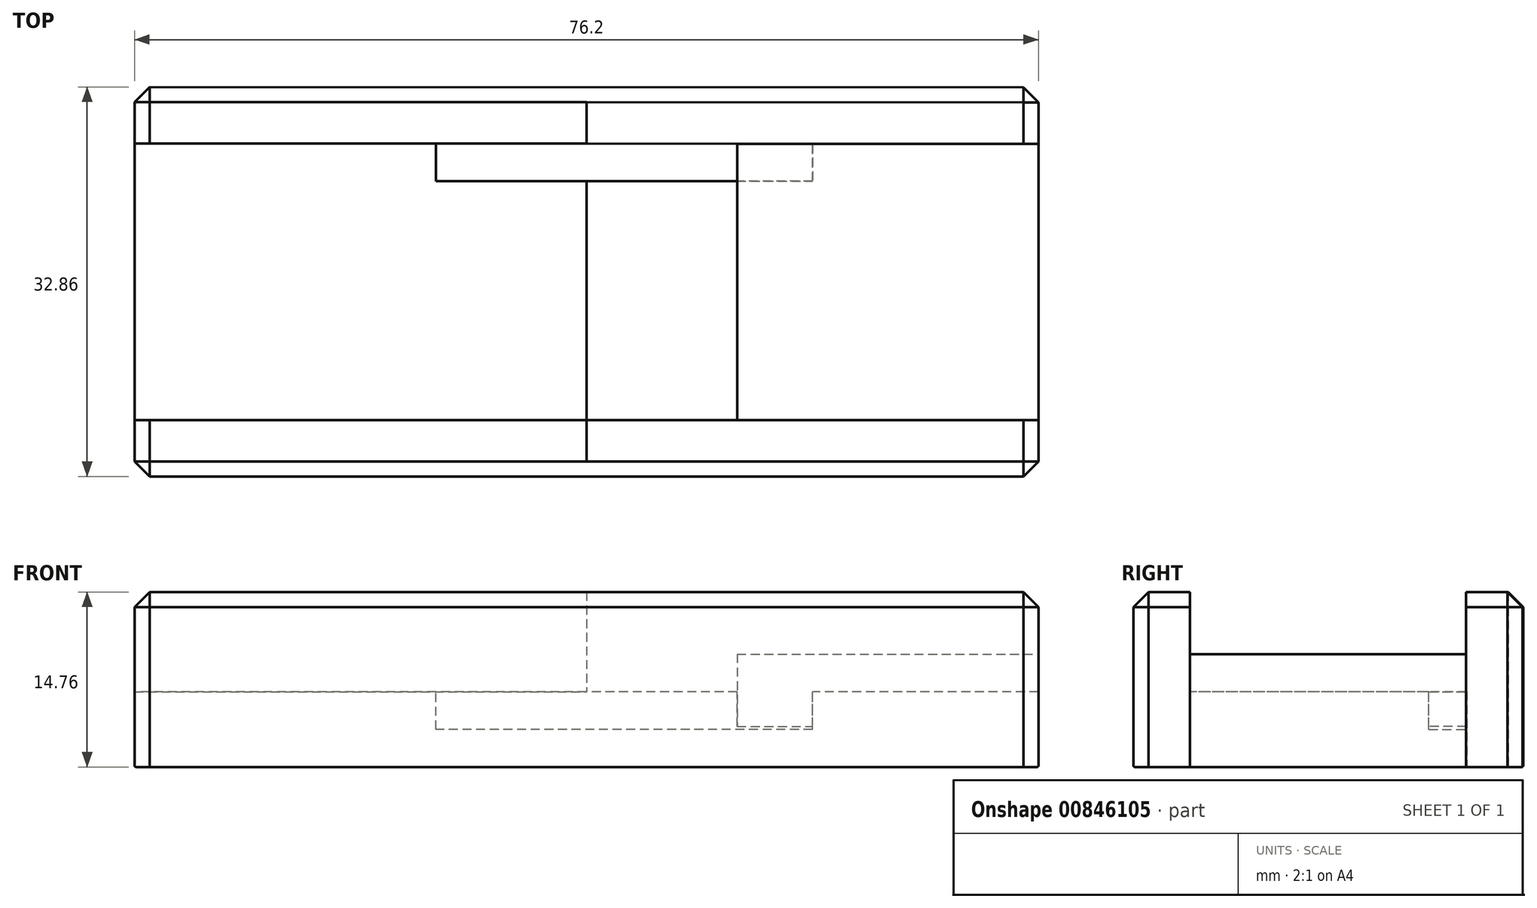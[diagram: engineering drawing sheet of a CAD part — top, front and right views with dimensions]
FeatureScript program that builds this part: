
annotation { "Feature Type Name" : "Feature", "Feature Type Description" : "" }
export const myFeature = defineFeature(function(context is Context, id is Id, definition is map)
    precondition{}
    {
        {
            assignVariable(context, id + "F0", {"name" : "EngravingDepth", "anyValue" : 0});
        }
        {
            var Q0;
            Q0=qCreatedBy(makeId("Top.planeOp"),FACE);
            var sketch = newSketch(context, id + "F1", { "sketchPlane" : qUnion([Q0])});
            skLineSegment(sketch, "E0", {"start": v(0, 0) * mm, "end": v(76.2, 0) * mm});
            skLineSegment(sketch, "E1", {"start": v(76.2, 0) * mm, "end": v(76.2, 23.3) * mm});
            skLineSegment(sketch, "E2", {"start": v(0, 23.34) * mm, "end": v(0, 0) * mm});
            skLineSegment(sketch, "E3", {"start": v(76.2, 23.3) * mm, "end": v(0, 23.34) * mm});
            skSolve(sketch);
        }
        {
            var Q0;
            Q0 = qSketchRegion(id + "F1", true);
            extrude(context, id + "F2", {"entities" : qUnion([Q0]), "depth" : 6.35 * mm, "offsetDistance" : 25.4 * mm});
        }
        {
            var Q0;
            Q0=makeQuery(id+"F2.opExtrude","CAP_FACE",FACE,{"disambiguationData":[OSD([sQuery(id+"F1.wireOp",EDGE,"E0"),sQuery(id+"F1.wireOp",EDGE,"E1"),sQuery(id+"F1.wireOp",EDGE,"E2"),sQuery(id+"F1.wireOp",EDGE,"E3")])],"isStart":false});
            var sketch = newSketch(context, id + "F3", { "sketchPlane" : qUnion([Q0])});
            skLineSegment(sketch, "E4", {"start": v(25.4, 20.14) * mm, "end": v(25.41, 37.06) * mm});
            skLineSegment(sketch, "E5", {"start": v(25.41, 37.06) * mm, "end": v(57.15, 37.04) * mm});
            skLineSegment(sketch, "E6", {"start": v(57.15, 20.14) * mm, "end": v(57.15, 37.04) * mm});
            skLineSegment(sketch, "E7", {"start": v(57.15, 20.14) * mm, "end": v(25.4, 20.14) * mm});
            skSolve(sketch);
        }
        {
            var Q0;
            Q0 = qSketchRegion(id + "F3", true);
            extrude(context, id + "F4", {"entities" : qUnion([Q0]), "operationType" : NewBodyOperationType.REMOVE, "oppositeDirection" : true, "depth" : 3.17 * mm, "offsetDistance" : 25.4 * mm});
        }
        {
            var Q0;
            Q0=makeQuery(id+"F2.opExtrude","CAP_FACE",FACE,{"disambiguationData":[OSD([sQuery(id+"F1.wireOp",EDGE,"E0"),sQuery(id+"F1.wireOp",EDGE,"E1"),sQuery(id+"F1.wireOp",EDGE,"E2"),sQuery(id+"F1.wireOp",EDGE,"E3")])],"isStart":false});
            var sketch = newSketch(context, id + "F5", { "sketchPlane" : qUnion([Q0])});
            skLineSegment(sketch, "E8.bottom", {"start": v(76.2, 0) * mm, "end": v(50.8, 0) * mm});
            skLineSegment(sketch, "E8.top", {"start": v(76.2, 23.3) * mm, "end": v(50.8, 23.3) * mm});
            skLineSegment(sketch, "E8.left", {"start": v(76.2, 0) * mm, "end": v(76.2, 23.3) * mm});
            skLineSegment(sketch, "E8.right", {"start": v(50.8, 0) * mm, "end": v(50.8, 23.3) * mm});
            skSolve(sketch);
        }
        {
            var Q0;
            Q0 = qSketchRegion(id + "F5", true);
            extrude(context, id + "F6", {"entities" : qUnion([Q0]), "depth" : 3.17 * mm, "offsetDistance" : 25.4 * mm});
        }
        {
            var Q0;
            Q0=makeQuery(id+"F6.opExtrude","CAP_FACE",FACE,{"disambiguationData":[OSD([sQuery(id+"F5.wireOp",EDGE,"E8.bottom"),sQuery(id+"F5.wireOp",EDGE,"E8.top"),sQuery(id+"F5.wireOp",EDGE,"E8.left"),sQuery(id+"F5.wireOp",EDGE,"E8.right")])],"isStart":false});
            var sketch = newSketch(context, id + "F7", { "sketchPlane" : qUnion([Q0])});
            skLineSegment(sketch, "E9.bottom", {"start": v(50.8, 23.3) * mm, "end": v(57.15, 23.3) * mm});
            skLineSegment(sketch, "E9.top", {"start": v(50.8, 20.12) * mm, "end": v(57.15, 20.12) * mm});
            skLineSegment(sketch, "E9.left", {"start": v(50.8, 23.3) * mm, "end": v(50.8, 20.12) * mm});
            skLineSegment(sketch, "E9.right", {"start": v(57.15, 23.3) * mm, "end": v(57.15, 20.12) * mm});
            skSolve(sketch);
        }
        {
            var Q0;
            Q0 = qSketchRegion(id + "F7", true);
            extrude(context, id + "F8", {"entities" : qUnion([Q0]), "operationType" : NewBodyOperationType.ADD, "oppositeDirection" : true, "depth" : 6.1 * mm, "offsetDistance" : 25.4 * mm});
        }
        {
            var Q0;
            Q0=makeQuery(id+"F2.opExtrude","SWEPT_FACE",FACE,{"disambiguationData":[OSD([sQuery(id+"F1.wireOp",EDGE,"E0")])]});
            var sketch = newSketch(context, id + "F9", { "sketchPlane" : qUnion([Q0])});
            skLineSegment(sketch, "E10.bottom", {"start": v(0, 0) * mm, "end": v(76.2, 0) * mm});
            skLineSegment(sketch, "E10.top", {"start": v(0, 14.76) * mm, "end": v(76.2, 14.76) * mm});
            skLineSegment(sketch, "E10.left", {"start": v(0, 0) * mm, "end": v(0, 14.76) * mm});
            skLineSegment(sketch, "E10.right", {"start": v(76.2, 0) * mm, "end": v(76.2, 14.76) * mm});
            skSolve(sketch);
        }
        {
            var Q0;
            Q0 = qSketchRegion(id + "F9", true);
            extrude(context, id + "F10", {"entities" : qUnion([Q0]), "depth" : 4.76 * mm, "offsetDistance" : 25.4 * mm});
        }
        {
            var Q0;
            Q0=makeQuery(id+"F10.opExtrude","CAP_EDGE",EDGE,{"disambiguationData":[OSD([sQuery(id+"F9.wireOp",EDGE,"E10.top")])],"isStart":false});
            var Q1;
            Q1=makeQuery(id+"F10.opExtrude","CAP_EDGE",EDGE,{"disambiguationData":[OSD([sQuery(id+"F9.wireOp",EDGE,"E10.right")])],"isStart":false});
            var Q2;
            Q2=makeQuery(id+"F10.opExtrude","SWEPT_EDGE",EDGE,{"disambiguationData":[OSD([sQuery(id+"F9.wireOp",EDGE,"E10.top"),sQuery(id+"F9.wireOp",EDGE,"E10.right")])]});
            var Q3;
            Q3=makeQuery(id+"F10.opExtrude","CAP_EDGE",EDGE,{"disambiguationData":[OSD([sQuery(id+"F9.wireOp",EDGE,"E10.left")])],"isStart":false});
            var Q4;
            Q4=makeQuery(id+"F10.opExtrude","SWEPT_EDGE",EDGE,{"disambiguationData":[OSD([sQuery(id+"F9.wireOp",EDGE,"E10.top"),sQuery(id+"F9.wireOp",EDGE,"E10.left")])]});
            chamfer(context, id + "F11", {"entities" : qUnion([Q0, Q1, Q2, Q3, Q4]), "width" : 1.27 * mm, "tangentPropagation" : true});
        }
        {
            var Q0;
            Q0=makeQuery(id+"F2.opExtrude","SWEPT_FACE",FACE,{"disambiguationData":[OSD([sQuery(id+"F1.wireOp",EDGE,"E3")])]});
            var sketch = newSketch(context, id + "F12", { "sketchPlane" : qUnion([Q0])});
            skLineSegment(sketch, "E11.bottom", {"start": v(-76.18, 0) * mm, "end": v(3.44, 0) * mm});
            skLineSegment(sketch, "E11.top", {"start": v(-76.18, 14.76) * mm, "end": v(3.44, 14.76) * mm});
            skLineSegment(sketch, "E11.left", {"start": v(-76.18, 0) * mm, "end": v(-76.18, 14.76) * mm});
            skLineSegment(sketch, "E11.right", {"start": v(3.44, 0) * mm, "end": v(3.44, 14.76) * mm});
            skSolve(sketch);
        }
        {
            var Q0;
            Q0 = qSketchRegion(id + "F12", true);
            extrude(context, id + "F13", {"entities" : qUnion([Q0]), "depth" : 4.76 * mm, "offsetDistance" : 25.4 * mm});
        }
        {
            var Q0;
            Q0=makeQuery(id+"F2.opExtrude","SWEPT_FACE",FACE,{"disambiguationData":[OSD([sQuery(id+"F1.wireOp",EDGE,"E1")])]});
            var sketch = newSketch(context, id + "F14", { "sketchPlane" : qUnion([Q0])});
            skLineSegment(sketch, "E12.bottom", {"start": v(15.12, 20.8) * mm, "end": v(36.76, 20.8) * mm});
            skLineSegment(sketch, "E12.top", {"start": v(15.12, -6.1) * mm, "end": v(36.76, -6.1) * mm});
            skLineSegment(sketch, "E12.left", {"start": v(15.12, 20.8) * mm, "end": v(15.12, -6.1) * mm});
            skLineSegment(sketch, "E12.right", {"start": v(36.76, 20.8) * mm, "end": v(36.76, -6.1) * mm});
            skSolve(sketch);
        }
        {
            var Q0;
            Q0 = qSketchRegion(id + "F14", true);
            extrude(context, id + "F15", {"entities" : qUnion([Q0]), "depth" : 3.17 * mm, "offsetDistance" : 25.4 * mm});
        }
        {
            var Q0;
            Q0=makeQuery(id+"F15.opExtrude","SWEPT_BODY",BODY,{"disambiguationData":[OSD([sQuery(id+"F14.wireOp",EDGE,"E12.bottom"),sQuery(id+"F14.wireOp",EDGE,"E12.top"),sQuery(id+"F14.wireOp",EDGE,"E12.left"),sQuery(id+"F14.wireOp",EDGE,"E12.right")])]});
            var Q1;
            Q1=makeQuery(id+"F13.opExtrude","SWEPT_BODY",BODY,{"disambiguationData":[OSD([sQuery(id+"F12.wireOp",EDGE,"E11.bottom"),sQuery(id+"F12.wireOp",EDGE,"E11.top"),sQuery(id+"F12.wireOp",EDGE,"E11.left"),sQuery(id+"F12.wireOp",EDGE,"E11.right")])]});
            booleanBodies(context, id + "F16", {"operationType" : BooleanOperationType.SUBTRACTION, "tools" : qUnion([Q0]), "targets" : qUnion([Q1])});
        }
        {
            var Q0;
            Q0=makeQuery(id+"F2.opExtrude","SWEPT_FACE",FACE,{"disambiguationData":[OSD([sQuery(id+"F1.wireOp",EDGE,"E2")])]});
            var sketch = newSketch(context, id + "F17", { "sketchPlane" : qUnion([Q0])});
            skLineSegment(sketch, "E13.bottom", {"start": v(-18.09, -4.86) * mm, "end": v(-37.56, -4.86) * mm});
            skLineSegment(sketch, "E13.top", {"start": v(-18.09, 23.73) * mm, "end": v(-37.56, 23.73) * mm});
            skLineSegment(sketch, "E13.left", {"start": v(-18.09, -4.86) * mm, "end": v(-18.09, 23.73) * mm});
            skLineSegment(sketch, "E13.right", {"start": v(-37.56, -4.86) * mm, "end": v(-37.56, 23.73) * mm});
            skSolve(sketch);
        }
        {
            var Q0;
            Q0 = qSketchRegion(id + "F17", true);
            extrude(context, id + "F18", {"entities" : qUnion([Q0]), "depth" : 6.35 * mm, "offsetDistance" : 25.4 * mm});
        }
        {
            var Q0;
            Q0=makeQuery(id+"F18.opExtrude","SWEPT_BODY",BODY,{"disambiguationData":[OSD([sQuery(id+"F17.wireOp",EDGE,"E13.bottom"),sQuery(id+"F17.wireOp",EDGE,"E13.top"),sQuery(id+"F17.wireOp",EDGE,"E13.left"),sQuery(id+"F17.wireOp",EDGE,"E13.right")])]});
            var Q1;
            Q1=makeQuery(id+"F13.opExtrude","SWEPT_BODY",BODY,{"disambiguationData":[OSD([sQuery(id+"F12.wireOp",EDGE,"E11.bottom"),sQuery(id+"F12.wireOp",EDGE,"E11.top"),sQuery(id+"F12.wireOp",EDGE,"E11.left"),sQuery(id+"F12.wireOp",EDGE,"E11.right")])]});
            booleanBodies(context, id + "F19", {"operationType" : BooleanOperationType.SUBTRACTION, "tools" : qUnion([Q0]), "targets" : qUnion([Q1])});
        }
        {
            var Q0;
            Q0=makeQuery(id+"F13.opExtrude","CAP_EDGE",EDGE,{"disambiguationData":[OSD([sQuery(id+"F12.wireOp",EDGE,"E11.left")])],"isStart":false});
            var Q1;
            Q1=makeQuery(id+"F13.opExtrude","CAP_EDGE",EDGE,{"disambiguationData":[OSD([sQuery(id+"F12.wireOp",EDGE,"E11.top")])],"isStart":false});
            var Q2;
            Q2=makeQuery(id+"F19.opBoolean","INTERSECT",EDGE,{"derivedFrom":[makeQuery(id+"F13.opExtrude","CAP_FACE",FACE,{"disambiguationData":[OSD([sQuery(id+"F12.wireOp",EDGE,"E11.bottom"),sQuery(id+"F12.wireOp",EDGE,"E11.top"),sQuery(id+"F12.wireOp",EDGE,"E11.left"),sQuery(id+"F12.wireOp",EDGE,"E11.right")])],"isStart":false}),makeQuery(id+"F18.opExtrude","CAP_FACE",FACE,{"disambiguationData":[OSD([sQuery(id+"F17.wireOp",EDGE,"E13.bottom"),sQuery(id+"F17.wireOp",EDGE,"E13.top"),sQuery(id+"F17.wireOp",EDGE,"E13.left"),sQuery(id+"F17.wireOp",EDGE,"E13.right")])],"isStart":true})]});
            var Q3;
            Q3=makeQuery(id+"F19.opBoolean","INTERSECT",EDGE,{"derivedFrom":[makeQuery(id+"F13.opExtrude","SWEPT_FACE",FACE,{"disambiguationData":[OSD([sQuery(id+"F12.wireOp",EDGE,"E11.top")])]}),makeQuery(id+"F18.opExtrude","CAP_FACE",FACE,{"disambiguationData":[OSD([sQuery(id+"F17.wireOp",EDGE,"E13.bottom"),sQuery(id+"F17.wireOp",EDGE,"E13.top"),sQuery(id+"F17.wireOp",EDGE,"E13.left"),sQuery(id+"F17.wireOp",EDGE,"E13.right")])],"isStart":true})]});
            var Q4;
            Q4=makeQuery(id+"F13.opExtrude","SWEPT_EDGE",EDGE,{"disambiguationData":[OSD([sQuery(id+"F12.wireOp",EDGE,"E11.top"),sQuery(id+"F12.wireOp",EDGE,"E11.left")])]});
            chamfer(context, id + "F20", {"entities" : qUnion([Q0, Q1, Q2, Q3, Q4]), "width" : 1.27 * mm, "tangentPropagation" : true});
        }
        {
            var Q0;
            Q0=qCreatedBy(makeId("Right.planeOp"),FACE);
            cPlane(context, id + "F21", {"entities" : qUnion([Q0]), "cplaneType" : CPlaneType.OFFSET, "offset" : 38.1 * mm, "width" : 152.4 * mm, "height" : 152.4 * mm});
        }
        {
            var Q0;
            Q0=qCreatedBy(id+"F21.planeOp",FACE);
            var sketch = newSketch(context, id + "F22", { "sketchPlane" : qUnion([Q0])});
            skLineSegment(sketch, "E14.right", {"start": v(23.3, 6.35) * mm, "end": v(23.3, 6.35) * mm});
            skLineSegment(sketch, "E15", {"start": v(0, 14.76) * mm, "end": v(-8.99, 14.76) * mm});
            skLineSegment(sketch, "E16", {"start": v(-8.99, 14.76) * mm, "end": v(-8.99, 22.15) * mm});
            skLineSegment(sketch, "E17", {"start": v(-8.99, 22.15) * mm, "end": v(31.53, 22.15) * mm});
            skLineSegment(sketch, "E18", {"start": v(31.53, 22.15) * mm, "end": v(31.53, 14.76) * mm});
            skLineSegment(sketch, "E19", {"start": v(23.32, 14.76) * mm, "end": v(31.53, 14.76) * mm});
            skLineSegment(sketch, "E20", {"start": v(0, 14.76) * mm, "end": v(0, 6.35) * mm});
            skLineSegment(sketch, "E21", {"start": v(0, 6.35) * mm, "end": v(23.32, 6.35) * mm});
            skLineSegment(sketch, "E22", {"start": v(23.32, 14.76) * mm, "end": v(23.32, 6.35) * mm});
            skSolve(sketch);
        }
        {
            var Q0;
            Q0=makeQuery(id+"F22.imprint","IMPRINT",FACE,{"disambiguationData":[TD([[makeQuery(id+"F22.imprint","IMPRINT",EDGE,{"derivedFrom":sQuery(id+"F22.wireOp",EDGE,"E15")}),-1.0]])]});
            extrude(context, id + "F23", {"entities" : qUnion([Q0]), "depth" : (getVariable(context, 'EngravingDepth') / 2) * mm, "offsetDistance" : 25.4 * mm, "hasDraft" : true, "draftAngle" : 45 * degree});
        }
        {
            var Q0;
            Q0=makeQuery(id+"F23.opExtrude","SWEPT_BODY",BODY,{"disambiguationData":[OSD([sQuery(id+"F22.wireOp",EDGE,"E14.bottom"),sQuery(id+"F22.wireOp",EDGE,"E14.left"),sQuery(id+"F22.wireOp",EDGE,"E14.right"),sQuery(id+"F22.wireOp",EDGE,"E15"),sQuery(id+"F22.wireOp",EDGE,"E16"),sQuery(id+"F22.wireOp",EDGE,"E17"),sQuery(id+"F22.wireOp",EDGE,"E18"),sQuery(id+"F22.wireOp",EDGE,"E19")])]});
            var Q1;
            Q1=makeQuery(id+"F23.opExtrude","CAP_FACE",FACE,{"disambiguationData":[OSD([sQuery(id+"F22.wireOp",EDGE,"E15"),sQuery(id+"F22.wireOp",EDGE,"E16"),sQuery(id+"F22.wireOp",EDGE,"E17"),sQuery(id+"F22.wireOp",EDGE,"E18"),sQuery(id+"F22.wireOp",EDGE,"E19"),sQuery(id+"F22.wireOp",EDGE,"E20"),sQuery(id+"F22.wireOp",EDGE,"E21"),sQuery(id+"F22.wireOp",EDGE,"1c44702a-84b8-4c98-ac38-a87e6212092e")])],"isStart":false});
            mirror(context, id + "F24", {"entities" : qUnion([Q0]), "mirrorPlane" : qUnion([Q1])});
        }
        {
            var Q0;
            Q0=makeQuery(id+"F24.opPattern","COPY",BODY,{"derivedFrom":makeQuery(id+"F23.opExtrude","SWEPT_BODY",BODY,{"disambiguationData":[OSD([sQuery(id+"F22.wireOp",EDGE,"E14.bottom"),sQuery(id+"F22.wireOp",EDGE,"E14.left"),sQuery(id+"F22.wireOp",EDGE,"E14.right"),sQuery(id+"F22.wireOp",EDGE,"E15"),sQuery(id+"F22.wireOp",EDGE,"E16"),sQuery(id+"F22.wireOp",EDGE,"E17"),sQuery(id+"F22.wireOp",EDGE,"E18"),sQuery(id+"F22.wireOp",EDGE,"E19")])]}),"instanceName":"1"});
            var Q1;
            Q1=makeQuery(id+"F23.opExtrude","SWEPT_BODY",BODY,{"disambiguationData":[OSD([sQuery(id+"F22.wireOp",EDGE,"E14.bottom"),sQuery(id+"F22.wireOp",EDGE,"E14.left"),sQuery(id+"F22.wireOp",EDGE,"E14.right"),sQuery(id+"F22.wireOp",EDGE,"E15"),sQuery(id+"F22.wireOp",EDGE,"E16"),sQuery(id+"F22.wireOp",EDGE,"E17"),sQuery(id+"F22.wireOp",EDGE,"E18"),sQuery(id+"F22.wireOp",EDGE,"E19")])]});
            var Q2;
            Q2=makeQuery(id+"F2.opExtrude","SWEPT_BODY",BODY,{"disambiguationData":[OSD([sQuery(id+"F1.wireOp",EDGE,"E0"),sQuery(id+"F1.wireOp",EDGE,"E1"),sQuery(id+"F1.wireOp",EDGE,"E2"),sQuery(id+"F1.wireOp",EDGE,"E3")])]});
            var Q3;
            Q3=makeQuery(id+"F10.opExtrude","SWEPT_BODY",BODY,{"disambiguationData":[OSD([sQuery(id+"F9.wireOp",EDGE,"E10.bottom"),sQuery(id+"F9.wireOp",EDGE,"E10.top"),sQuery(id+"F9.wireOp",EDGE,"E10.left"),sQuery(id+"F9.wireOp",EDGE,"E10.right")])]});
            var Q4;
            Q4=makeQuery(id+"F13.opExtrude","SWEPT_BODY",BODY,{"disambiguationData":[OSD([sQuery(id+"F12.wireOp",EDGE,"E11.bottom"),sQuery(id+"F12.wireOp",EDGE,"E11.top"),sQuery(id+"F12.wireOp",EDGE,"E11.left"),sQuery(id+"F12.wireOp",EDGE,"E11.right")])]});
            booleanBodies(context, id + "F25", {"operationType" : BooleanOperationType.SUBTRACTION, "tools" : qUnion([Q0, Q1]), "targets" : qUnion([Q2, Q3, Q4])});
        }
        {
            var Q0;
            Q0=makeQuery(id+"F2.opExtrude","CAP_EDGE",EDGE,{"disambiguationData":[OSD([sQuery(id+"F1.wireOp",EDGE,"E1")])],"isStart":true});
            var Q1;
            Q1=makeQuery(id+"F13.opExtrude","SWEPT_EDGE",EDGE,{"disambiguationData":[OSD([sQuery(id+"F12.wireOp",EDGE,"E11.bottom"),sQuery(id+"F12.wireOp",EDGE,"E11.left")])]});
            var Q2;
            Q2=makeQuery(id+"F20.opChamfer","BLEND_EDGE",EDGE,{"blendedFrom":[makeQuery(id+"F13.opExtrude","CAP_EDGE",EDGE,{"disambiguationData":[OSD([sQuery(id+"F12.wireOp",EDGE,"E11.left")])],"isStart":false}),makeQuery(id+"F13.opExtrude","SWEPT_FACE",FACE,{"disambiguationData":[OSD([sQuery(id+"F12.wireOp",EDGE,"E11.bottom")])]})],"blendedInto":[makeQuery(id+"F13.opExtrude","SWEPT_FACE",FACE,{"disambiguationData":[OSD([sQuery(id+"F12.wireOp",EDGE,"E11.bottom")])]})]});
            var Q3;
            Q3=makeQuery(id+"F13.opExtrude","CAP_EDGE",EDGE,{"disambiguationData":[OSD([sQuery(id+"F12.wireOp",EDGE,"E11.bottom")])],"isStart":false});
            var Q4;
            {var subQ0=sQuery(id+"F12.wireOp",EDGE,"E11.bottom");Q4=makeQuery(id+"F20.opChamfer","BLEND_EDGE",EDGE,{"blendedFrom":[makeQuery(id+"F19.opBoolean","INTERSECT",EDGE,{"derivedFrom":[makeQuery(id+"F13.opExtrude","CAP_FACE",FACE,{"disambiguationData":[OSD([subQ0,sQuery(id+"F12.wireOp",EDGE,"E11.top"),sQuery(id+"F12.wireOp",EDGE,"E11.left"),sQuery(id+"F12.wireOp",EDGE,"E11.right")])],"isStart":false}),makeQuery(id+"F18.opExtrude","CAP_FACE",FACE,{"disambiguationData":[OSD([sQuery(id+"F17.wireOp",EDGE,"E13.bottom"),sQuery(id+"F17.wireOp",EDGE,"E13.top"),sQuery(id+"F17.wireOp",EDGE,"E13.left"),sQuery(id+"F17.wireOp",EDGE,"E13.right")])],"isStart":true})]}),makeQuery(id+"F13.opExtrude","SWEPT_FACE",FACE,{"disambiguationData":[OSD([subQ0])]})],"blendedInto":[makeQuery(id+"F13.opExtrude","SWEPT_FACE",FACE,{"disambiguationData":[OSD([subQ0])]})]});}
            var Q5;
            Q5=makeQuery(id+"F19.opBoolean","INTERSECT",EDGE,{"derivedFrom":[makeQuery(id+"F13.opExtrude","SWEPT_FACE",FACE,{"disambiguationData":[OSD([sQuery(id+"F12.wireOp",EDGE,"E11.bottom")])]}),makeQuery(id+"F18.opExtrude","CAP_FACE",FACE,{"disambiguationData":[OSD([sQuery(id+"F17.wireOp",EDGE,"E13.bottom"),sQuery(id+"F17.wireOp",EDGE,"E13.top"),sQuery(id+"F17.wireOp",EDGE,"E13.left"),sQuery(id+"F17.wireOp",EDGE,"E13.right")])],"isStart":true})]});
            var Q6;
            Q6=makeQuery(id+"F2.opExtrude","CAP_EDGE",EDGE,{"disambiguationData":[OSD([sQuery(id+"F1.wireOp",EDGE,"E2")])],"isStart":true});
            var Q7;
            Q7=makeQuery(id+"F10.opExtrude","SWEPT_EDGE",EDGE,{"disambiguationData":[OSD([sQuery(id+"F9.wireOp",EDGE,"E10.bottom"),sQuery(id+"F9.wireOp",EDGE,"E10.left")])]});
            var Q8;
            Q8=makeQuery(id+"F11.opChamfer","BLEND_EDGE",EDGE,{"blendedFrom":[makeQuery(id+"F10.opExtrude","CAP_EDGE",EDGE,{"disambiguationData":[OSD([sQuery(id+"F9.wireOp",EDGE,"E10.left")])],"isStart":false}),makeQuery(id+"F10.opExtrude","SWEPT_FACE",FACE,{"disambiguationData":[OSD([sQuery(id+"F9.wireOp",EDGE,"E10.bottom")])]})],"blendedInto":[makeQuery(id+"F10.opExtrude","SWEPT_FACE",FACE,{"disambiguationData":[OSD([sQuery(id+"F9.wireOp",EDGE,"E10.bottom")])]})]});
            var Q9;
            Q9=makeQuery(id+"F10.opExtrude","CAP_EDGE",EDGE,{"disambiguationData":[OSD([sQuery(id+"F9.wireOp",EDGE,"E10.bottom")])],"isStart":false});
            var Q10;
            Q10=makeQuery(id+"F11.opChamfer","BLEND_EDGE",EDGE,{"blendedFrom":[makeQuery(id+"F10.opExtrude","CAP_EDGE",EDGE,{"disambiguationData":[OSD([sQuery(id+"F9.wireOp",EDGE,"E10.right")])],"isStart":false}),makeQuery(id+"F10.opExtrude","SWEPT_FACE",FACE,{"disambiguationData":[OSD([sQuery(id+"F9.wireOp",EDGE,"E10.bottom")])]})],"blendedInto":[makeQuery(id+"F10.opExtrude","SWEPT_FACE",FACE,{"disambiguationData":[OSD([sQuery(id+"F9.wireOp",EDGE,"E10.bottom")])]})]});
            var Q11;
            Q11=makeQuery(id+"F10.opExtrude","SWEPT_EDGE",EDGE,{"disambiguationData":[OSD([sQuery(id+"F9.wireOp",EDGE,"E10.bottom"),sQuery(id+"F9.wireOp",EDGE,"E10.right")])]});
            fillet(context, id + "F26", {"entities" : qUnion([Q0, Q1, Q2, Q3, Q4, Q5, Q6, Q7, Q8, Q9, Q10, Q11]), "radius" : 0.13 * mm, "tangentPropagation" : true, "allowEdgeOverflow" : false});
        }
    });
